annotation { "Feature Type Name" : "Feature", "Feature Type Description" : "" }
export const myFeature = defineFeature(function(context is Context, id is Id, definition is map)
    precondition{}
    {
        {
            var Q0;
            Q0=qCreatedBy(makeId("Top.planeOp"),FACE);
            var sketch = newSketch(context, id + "F0", { "sketchPlane" : qUnion([Q0])});
            skLineSegment(sketch, "E0.bottom", {"start": v(-60.84, -57.46) * mm, "end": v(15.36, -57.46) * mm});
            skLineSegment(sketch, "E0.top", {"start": v(-60.84, 56.84) * mm, "end": v(15.36, 56.84) * mm});
            skLineSegment(sketch, "E0.left", {"start": v(-60.84, -57.46) * mm, "end": v(-60.84, 56.84) * mm});
            skLineSegment(sketch, "E0.right", {"start": v(15.36, -57.46) * mm, "end": v(15.36, 56.84) * mm});
            skSolve(sketch);
        }
        {
            var Q0;
            Q0=makeQuery(id+"F0.imprint","IMPRINT",FACE,{"disambiguationData":[TD([[makeQuery(id+"F0.imprint","IMPRINT",EDGE,{"derivedFrom":sQuery(id+"F0.wireOp",EDGE,"E0.bottom")}),1.0]])]});
            extrude(context, id + "F1", {"entities" : qUnion([Q0]), "depth" : 3.17 * mm});
        }
        {
            var Q0;
            Q0=makeQuery(id+"F1.opExtrude","CAP_FACE",FACE,{"disambiguationData":[OSD([sQuery(id+"F0.wireOp",EDGE,"E0.bottom"),sQuery(id+"F0.wireOp",EDGE,"E0.top"),sQuery(id+"F0.wireOp",EDGE,"E0.left"),sQuery(id+"F0.wireOp",EDGE,"E0.right")])],"isStart":false});
            var sketch = newSketch(context, id + "F2", { "sketchPlane" : qUnion([Q0])});
            skText(sketch, "E1", { "text": "STEM Academy", "fontName": "AllertaStencil-Regular.ttf"});
            skText(sketch, "E2", { "text": "Hall Pass", "fontName": "AllertaStencil-Regular.ttf"});
            const initialGuessF2  = {"E1": [-0.05746, 0.0306, 1, 0, 0.00671], "E2": [-0.04054, 0.01691, 1, 0, 0.00618]};
            skSetInitialGuess(sketch, initialGuessF2);
            skSolve(sketch);
        }
        {
            var Q0;
            Q0 = qSketchRegion(id + "F2", true);
            extrude(context, id + "F3", {"entities" : qUnion([Q0]), "operationType" : NewBodyOperationType.REMOVE, "oppositeDirection" : true, "depth" : 25.4 * mm});
        }
        {
            var Q0;
            Q0=makeQuery(id+"F1.opExtrude","CAP_FACE",FACE,{"disambiguationData":[OSD([sQuery(id+"F0.wireOp",EDGE,"E0.bottom"),sQuery(id+"F0.wireOp",EDGE,"E0.top"),sQuery(id+"F0.wireOp",EDGE,"E0.left"),sQuery(id+"F0.wireOp",EDGE,"E0.right")])],"isStart":false});
            var sketch = newSketch(context, id + "F4", { "sketchPlane" : qUnion([Q0])});
            skFitSpline(sketch, "E3", {"points": [v(-38.7, -8.75) * mm, v(-37.37, -6.57) * mm, v(-35.66, -3.53) * mm, v(-34.43, -1.26) * mm, v(-32.72, 1.5) * mm, v(-31.4, 2.34) * mm, v(-30.07, 2.72) * mm, v(-28.27, 2.82) * mm, v(-26.37, 2.34) * mm, v(-24.57, 0.92) * mm, v(-22.77, -1.26) * mm, v(-21.16, -3.82) * mm, v(-20.21, -5.52) * mm, v(-18.4, -8.37) * mm, v(-17.94, -9.88) * mm, v(-17.18, -10.64) * mm, v(-18.6, -11.3) * mm, v(-20.21, -12.25) * mm, v(-21.54, -13.1) * mm, v(-19.26, -13.1) * mm, v(-17.27, -13.1) * mm, v(-12.72, -12.92) * mm, v(-10.07, -12.63) * mm, v(-9.02, -12.54) * mm, v(-8.08, -10.83) * mm, v(-7.03, -8.94) * mm, v(-5.7, -6.38) * mm, v(-4.85, -4.96) * mm, v(-3.81, -3.25) * mm, v(-3.53, -2.11) * mm, v(-5.42, -3.44) * mm, v(-7.22, -3.91) * mm, v(-7.8, -4.1) * mm, v(-8.74, -2.11) * mm, v(-9.5, -0.69) * mm, v(-10.64, 1.2) * mm, v(-11.87, 2.34) * mm, v(-13.95, 2.82) * mm, v(-17.65, 2.82) * mm, v(-20.59, 2.82) * mm, v(-23.53, 2.82) * mm, v(-25.61, 2.82) * mm, v(-28.25, 2.83) * mm], "startDerivative": vector(49, 78.62) * mm, "endDerivative": vector(-104.24, 0.34) * mm});
            skFitSpline(sketch, "E4", {"points": [v(-38.7, -8.75) * mm, v(-35.9, -10.53) * mm, v(-34.46, -11.5) * mm, v(-32.65, -12.34) * mm, v(-30.41, -13.49) * mm, v(-28.72, -14.4) * mm, v(-28.12, -14.82) * mm, v(-27.33, -13.97) * mm, v(-26.37, -12.22) * mm, v(-24.97, -9.74) * mm, v(-24, -8.07) * mm, v(-23.16, -6.57) * mm, v(-22.26, -4.73) * mm, v(-21.5, -3.21) * mm], "startDerivative": vector(30.17, -18.72) * mm, "endDerivative": vector(10.05, 20.2) * mm});
            skFitSpline(sketch, "E5", {"points": [v(-21.16, -35.54) * mm, v(-19.73, -33.17) * mm, v(-18.77, -31.25) * mm, v(-16.33, -26.8) * mm, v(-15.45, -25.15) * mm, v(-15.02, -24.63) * mm, v(-15.02, -27.15) * mm, v(-15.02, -28.46) * mm, v(-15.02, -29.6) * mm, v(-13.8, -29.68) * mm, v(-10.22, -29.68) * mm, v(-8.04, -29.77) * mm, v(-6.9, -29.77) * mm, v(-7.35, -28.55) * mm, v(-8.74, -26.1) * mm, v(-10.48, -22.97) * mm, v(-12.05, -20) * mm, v(-12.72, -18.35) * mm, v(-11.62, -17.39) * mm, v(-8.83, -15.65) * mm, v(-5.86, -13.99) * mm, v(-4.12, -12.92) * mm, v(-2.9, -12.34) * mm, v(-1.77, -12.92) * mm, v(-0.9, -14.6) * mm, v(0, -16.6) * mm, v(1.63, -19.3) * mm, v(2.77, -21.4) * mm, v(3.38, -24.1) * mm, v(2.5, -27.33) * mm, v(0.94, -28.99) * mm, v(-2.46, -29.94) * mm, v(-4.64, -29.77) * mm, v(-6.92, -29.8) * mm], "startDerivative": vector(47.12, 74.8) * mm, "endDerivative": vector(-76.8, -4.2) * mm});
            skFitSpline(sketch, "E6", {"points": [v(-21.16, -35.54) * mm, v(-20.18, -36.83) * mm, v(-19.32, -38.43) * mm, v(-18.45, -39.83) * mm, v(-17.47, -41.6) * mm, v(-16.05, -43.78) * mm, v(-15.28, -44.99) * mm, v(-14.95, -43.57) * mm, v(-14.85, -41.6) * mm, v(-14.85, -41.16) * mm, v(-12.72, -41.27) * mm, v(-10.7, -41.27) * mm, v(-8.62, -41.27) * mm, v(-7.3, -40.94) * mm, v(-5.78, -39.85) * mm, v(-4.03, -37.56) * mm, v(-2.94, -35.54) * mm, v(-1.84, -34.06) * mm, v(0, -31.1) * mm, v(0.94, -28.99) * mm], "startDerivative": vector(21.1, -25.14) * mm, "endDerivative": vector(13.43, 34.29) * mm});
            skFitSpline(sketch, "E7", {"points": [v(-35.23, -14.04) * mm, v(-34.53, -15.24) * mm, v(-33.4, -16.92) * mm, v(-32, -19.17) * mm, v(-30.25, -21.91) * mm, v(-29.12, -23.8) * mm, v(-28.56, -24.65) * mm, v(-30.6, -23.46) * mm, v(-32.65, -22.47) * mm, v(-33.27, -22.05) * mm, v(-34.11, -23.46) * mm, v(-35.66, -26.2) * mm, v(-37.37, -28.99) * mm, v(-36.43, -28.99) * mm, v(-33.62, -28.99) * mm, v(-30.8, -28.99) * mm, v(-27.33, -28.99) * mm, v(-24.48, -28.99) * mm, v(-23.92, -28.99) * mm, v(-23.85, -30.48) * mm, v(-23.92, -32.73) * mm, v(-23.92, -35.54) * mm, v(-23.92, -40.46) * mm, v(-23.92, -41.3) * mm, v(-25.33, -41.38) * mm, v(-27.33, -41.59) * mm, v(-29.26, -41.52) * mm, v(-31.93, -41.45) * mm, v(-34.46, -41.59) * mm, v(-36.5, -41.1) * mm, v(-38.27, -40.25) * mm, v(-39.52, -38.57) * mm, v(-40.08, -36.95) * mm, v(-40.36, -35.54) * mm, v(-39.87, -34) * mm, v(-38.7, -31.4) * mm, v(-37.37, -29.5) * mm, v(-36.42, -28.99) * mm], "startDerivative": vector(29.24, -52.07) * mm, "endDerivative": vector(48.59, 18.65) * mm});
            skFitSpline(sketch, "E8", {"points": [v(-35.23, -14.04) * mm, v(-37.37, -14.04) * mm, v(-39.53, -14.04) * mm, v(-41.76, -14.04) * mm, v(-44.05, -14.04) * mm, v(-46.47, -14.04) * mm, v(-45.83, -14.77) * mm, v(-44.56, -15.6) * mm, v(-43.73, -16.04) * mm, v(-43.16, -16.36) * mm, v(-43.8, -17.25) * mm, v(-44.94, -19.03) * mm, v(-46.09, -21.07) * mm, v(-46.53, -22.08) * mm, v(-46.78, -23.42) * mm, v(-46.53, -24.88) * mm, v(-45.64, -26.54) * mm, v(-44.56, -28.99) * mm, v(-43.48, -30.8) * mm, v(-42.46, -32.45) * mm, v(-40.36, -35.54) * mm], "startDerivative": vector(-39.11, 0.03) * mm, "endDerivative": vector(31.98, -46.13) * mm});
            skFitSpline(sketch, "E9", {"points": [v(-27.33, 2.82) * mm, v(-28.27, 2.82) * mm], "startDerivative": vector(-0.94, 0) * mm, "endDerivative": vector(-0.94, 0) * mm});
            skFitSpline(sketch, "E10", {"points": [v(-6.14, -29.75) * mm, v(-6.9, -29.77) * mm], "startDerivative": vector(-0.77, -0.02) * mm, "endDerivative": vector(-0.77, -0.02) * mm});
            skFitSpline(sketch, "E11", {"points": [v(-37.37, -28.99) * mm, v(-37.37, -29.5) * mm], "startDerivative": vector(0, -0.52) * mm, "endDerivative": vector(0, -0.52) * mm});
            skFitSpline(sketch, "E12", {"points": [v(-41.14, -34.43) * mm, v(-40.36, -35.54) * mm], "startDerivative": vector(0.77, -1.11) * mm, "endDerivative": vector(0.77, -1.11) * mm});
            skFitSpline(sketch, "E13", {"points": [v(-6.9, -29.77) * mm, v(-6.14, -29.75) * mm], "startDerivative": vector(0.77, 0.02) * mm, "endDerivative": vector(0.77, 0.02) * mm});
            skFitSpline(sketch, "E14", {"points": [v(-6.9, -29.77) * mm, v(-6.14, -29.75) * mm, v(-4.64, -29.77) * mm], "startDerivative": vector(1.7, 0.06) * mm, "endDerivative": vector(2.78, -0.05) * mm});
            skFitSpline(sketch, "E15", {"points": [v(0, -31.1) * mm, v(0.68, -29.65) * mm, v(0.94, -28.99) * mm], "startDerivative": vector(1.27, 2.66) * mm, "endDerivative": vector(0.56, 1.5) * mm});
            skSolve(sketch);
        }
        {
            var Q0;
            {var subQ2=sQuery(id+"F4.wireOp",EDGE,"E9");Q0=makeQuery(id+"F4.imprint","IMPRINT",FACE,{"disambiguationData":[TD([[makeQuery(id+"F4.imprint","IMPRINT",EDGE,{"derivedFrom":subQ2}),1.0]])]});}
            var Q1;
            {var subQ0=sQuery(id+"F4.wireOp",EDGE,"E4");Q1=makeQuery(id+"F4.imprint","IMPRINT",FACE,{"disambiguationData":[TD([[makeQuery(id+"F4.imprint","IMPRINT",EDGE,{"derivedFrom":subQ0}),1.0]])]});}
            extrude(context, id + "F5", {"entities" : qUnion([Q0, Q1]), "operationType" : NewBodyOperationType.REMOVE, "depth" : 25.4 * mm});
        }
        {
            var Q0;
            Q0 = qSketchRegion(id + "F4", true);
            extrude(context, id + "F6", {"entities" : qUnion([Q0]), "operationType" : NewBodyOperationType.REMOVE, "oppositeDirection" : true, "depth" : 25.4 * mm});
        }
        {
            var Q0;
            {var subQ9=sQuery(id+"F4.wireOp",EDGE,"E4");Q0=makeQuery(id+"F4.imprint","IMPRINT",FACE,{"disambiguationData":[TD([[makeQuery(id+"F4.imprint","IMPRINT",EDGE,{"derivedFrom":subQ9}),-1.0]])]});}
            var sketch = newSketch(context, id + "F7", { "sketchPlane" : qUnion([Q0])});
            skCircle(sketch, "E16", {"center": v(-23.31, 46.91) * mm, "radius": 3.37 * mm});
            skSolve(sketch);
        }
        {
            var Q0;
            Q0 = qSketchRegion(id + "F7", true);
            extrude(context, id + "F8", {"entities" : qUnion([Q0]), "operationType" : NewBodyOperationType.REMOVE, "oppositeDirection" : true, "depth" : 25.4 * mm});
        }
        {
            var Q0;
            Q0=makeQuery(id+"F1.opExtrude","CAP_EDGE",EDGE,{"disambiguationData":[OSD([sQuery(id+"F0.wireOp",EDGE,"E0.left")])],"isStart":false});
            var Q1;
            Q1=makeQuery(id+"F1.opExtrude","CAP_EDGE",EDGE,{"disambiguationData":[OSD([sQuery(id+"F0.wireOp",EDGE,"E0.top")])],"isStart":false});
            var Q2;
            Q2=makeQuery(id+"F1.opExtrude","CAP_EDGE",EDGE,{"disambiguationData":[OSD([sQuery(id+"F0.wireOp",EDGE,"E0.right")])],"isStart":false});
            var Q3;
            Q3=makeQuery(id+"F1.opExtrude","CAP_EDGE",EDGE,{"disambiguationData":[OSD([sQuery(id+"F0.wireOp",EDGE,"E0.bottom")])],"isStart":false});
            fillet(context, id + "F9", {"entities" : qUnion([Q0, Q1, Q2, Q3]), "radius" : 1.27 * mm, "tangentPropagation" : true, "allowEdgeOverflow" : false});
        }
    });